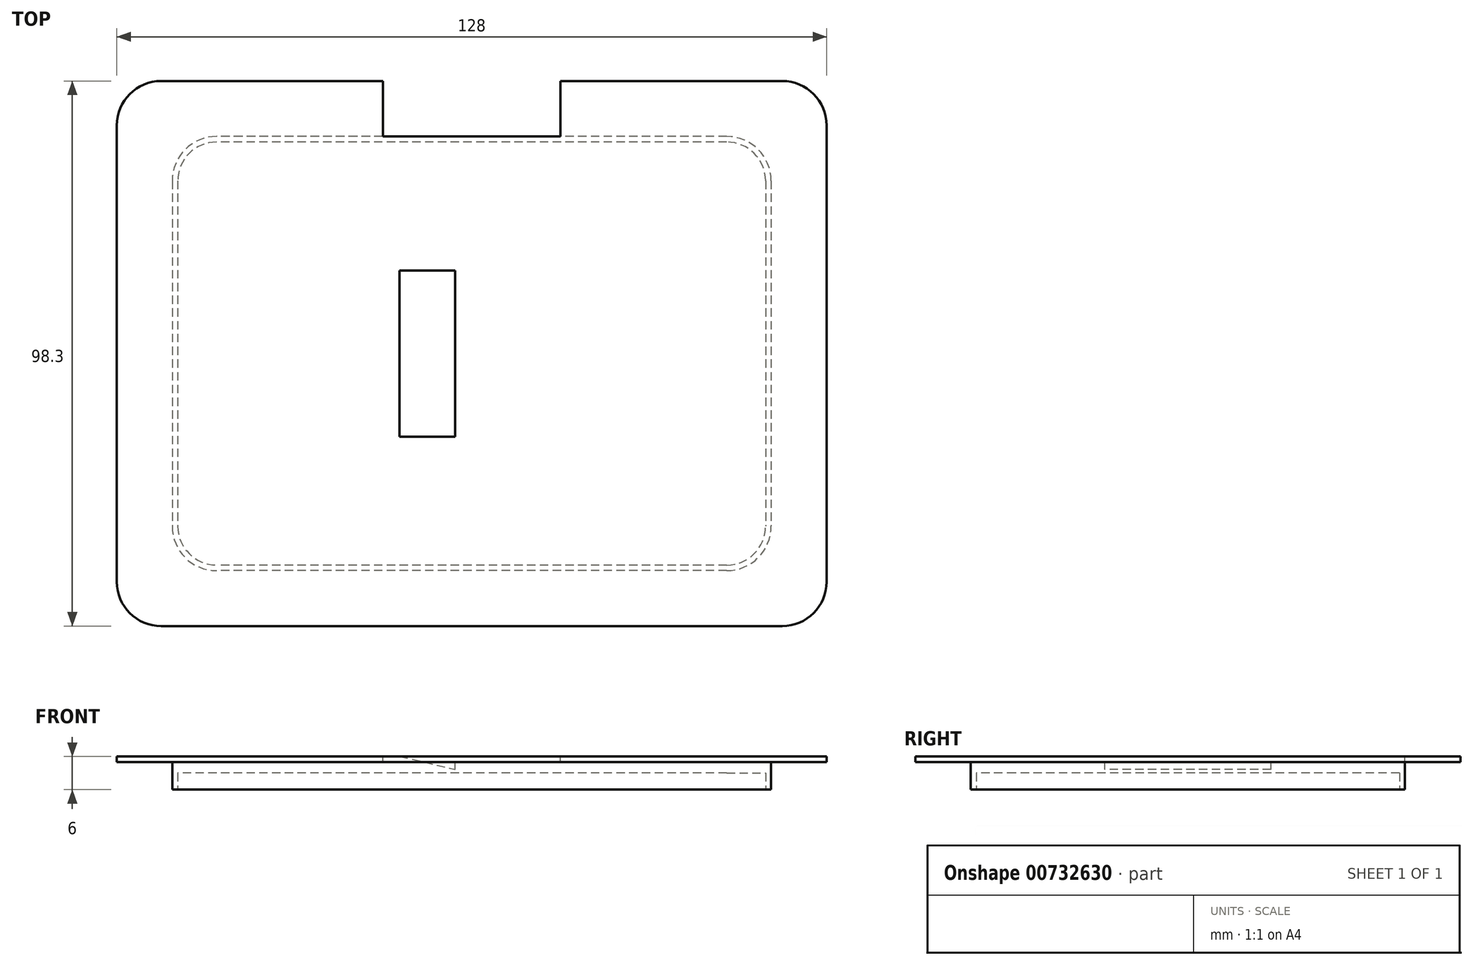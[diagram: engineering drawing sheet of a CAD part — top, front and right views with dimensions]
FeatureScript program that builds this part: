
annotation { "Feature Type Name" : "Feature", "Feature Type Description" : "" }
export const myFeature = defineFeature(function(context is Context, id is Id, definition is map)
    precondition{}
    {
        {
            var Q0;
            Q0=qCreatedBy(makeId("Top.planeOp"),FACE);
            var sketch = newSketch(context, id + "F0", { "sketchPlane" : qUnion([Q0])});
            skLineSegment(sketch, "E0.bottom", {"start": v(54, 39.15) * mm, "end": v(-54, 39.15) * mm});
            skLineSegment(sketch, "E0.top", {"start": v(54, -39.15) * mm, "end": v(-54, -39.15) * mm});
            skLineSegment(sketch, "E0.left", {"start": v(54, 39.15) * mm, "end": v(54, -39.15) * mm});
            skLineSegment(sketch, "E0.right", {"start": v(-54, 39.15) * mm, "end": v(-54, -39.15) * mm});
            skPoint(sketch, "E0.middle", {"position": v(0, 0) * mm});
            skLineSegment(sketch, "E1.0", {"start": v(64, 49.15) * mm, "end": v(-64, 49.15) * mm});
            skLineSegment(sketch, "E1.1", {"start": v(64, 49.15) * mm, "end": v(64, -49.15) * mm});
            skLineSegment(sketch, "E1.2", {"start": v(64, -49.15) * mm, "end": v(-64, -49.15) * mm});
            skLineSegment(sketch, "E1.3", {"start": v(-64, 49.15) * mm, "end": v(-64, -49.15) * mm});
            skLineSegment(sketch, "E2.bottom", {"start": v(-3, 15) * mm, "end": v(-13, 15) * mm});
            skLineSegment(sketch, "E2.top", {"start": v(-3, -15) * mm, "end": v(-13, -15) * mm});
            skLineSegment(sketch, "E2.left", {"start": v(-3, 15) * mm, "end": v(-3, -15) * mm});
            skLineSegment(sketch, "E2.right", {"start": v(-13, 15) * mm, "end": v(-13, -15) * mm});
            skPoint(sketch, "E2.middle", {"position": v(-8, 0) * mm});
            skSolve(sketch);
        }
        {
            var Q0;
            Q0=makeQuery(id+"F0.imprint","IMPRINT",FACE,{"disambiguationData":[TD([[makeQuery(id+"F0.imprint","IMPRINT",EDGE,{"derivedFrom":sQuery(id+"F0.wireOp",EDGE,"E0.bottom")}),-1.0]])]});
            var Q1;
            Q1=makeQuery(id+"F0.imprint","IMPRINT",FACE,{"disambiguationData":[TD([[makeQuery(id+"F0.imprint","IMPRINT",EDGE,{"derivedFrom":sQuery(id+"F0.wireOp",EDGE,"E0.bottom")}),1.0]])]});
            var Q2;
            Q2=makeQuery(id+"F0.imprint","IMPRINT",FACE,{"disambiguationData":[TD([[makeQuery(id+"F0.imprint","IMPRINT",EDGE,{"derivedFrom":sQuery(id+"F0.wireOp",EDGE,"E2.bottom")}),1.0]])]});
            extrude(context, id + "F1", {"entities" : qUnion([Q0, Q1, Q2]), "depth" : 1 * mm, "offsetDistance" : 25 * mm});
        }
        {
            var Q0;
            Q0=makeQuery(id+"F0.imprint","IMPRINT",FACE,{"disambiguationData":[TD([[makeQuery(id+"F0.imprint","IMPRINT",EDGE,{"derivedFrom":sQuery(id+"F0.wireOp",EDGE,"E0.bottom")}),1.0]])]});
            var Q1;
            Q1=makeQuery(id+"F0.imprint","IMPRINT",FACE,{"disambiguationData":[TD([[makeQuery(id+"F0.imprint","IMPRINT",EDGE,{"derivedFrom":sQuery(id+"F0.wireOp",EDGE,"E2.bottom")}),1.0]])]});
            extrude(context, id + "F2", {"entities" : qUnion([Q0, Q1]), "operationType" : NewBodyOperationType.ADD, "oppositeDirection" : true, "depth" : 5 * mm, "offsetDistance" : 25 * mm});
        }
        {
            var Q0;
            Q0=makeQuery(id+"F0.imprint","IMPRINT",FACE,{"disambiguationData":[TD([[makeQuery(id+"F0.imprint","IMPRINT",EDGE,{"derivedFrom":sQuery(id+"F0.wireOp",EDGE,"E2.bottom")}),1.0]])]});
            extrude(context, id + "F3", {"entities" : qUnion([Q0]), "operationType" : NewBodyOperationType.REMOVE, "endBound" : BoundingType.SYMMETRIC, "oppositeDirection" : true, "depth" : 5 * mm, "offsetDistance" : 25 * mm});
        }
        {
            var Q0;
            Q0=makeQuery(id+"F3.boolean.opBoolean","COPY",EDGE,{"derivedFrom":makeQuery(id+"F3.opExtrude","CAP_EDGE",EDGE,{"disambiguationData":[OSD([sQuery(id+"F0.wireOp",EDGE,"E2.right")])],"isStart":false})});
            chamfer(context, id + "F4", {"entities" : qUnion([Q0]), "chamferType" : ChamferType.TWO_OFFSETS, "width1" : 15 * mm, "oppositeDirection" : false, "width2" : 3.5 * mm, "tangentPropagation" : true});
        }
        {
            var Q0;
            Q0=makeQuery(id+"F2.opExtrude","CAP_FACE",FACE,{"disambiguationData":[OSD([sQuery(id+"F0.wireOp",EDGE,"E0.bottom"),sQuery(id+"F0.wireOp",EDGE,"E0.top"),sQuery(id+"F0.wireOp",EDGE,"E0.left"),sQuery(id+"F0.wireOp",EDGE,"E0.right")])],"isStart":false});
            var sketch = newSketch(context, id + "F5", { "sketchPlane" : qUnion([Q0])});
            skArc(sketch, "E3.0", {"start": v(46, -38.15) * mm, "mid": v(50.95, -36.1) * mm, "end": v(53, -31.15) * mm});
            skLineSegment(sketch, "E3.1", {"start": v(53, -31.15) * mm, "end": v(53, 31.15) * mm});
            skLineSegment(sketch, "E3.2", {"start": v(46, -38.15) * mm, "end": v(-46, -38.15) * mm});
            skArc(sketch, "E3.3", {"start": v(53, 31.15) * mm, "mid": v(50.95, 36.1) * mm, "end": v(46, 38.15) * mm});
            skArc(sketch, "E3.4", {"start": v(-53, -31.15) * mm, "mid": v(-50.95, -36.1) * mm, "end": v(-46, -38.15) * mm});
            skLineSegment(sketch, "E3.5", {"start": v(-53, -31.15) * mm, "end": v(-53, 31.15) * mm});
            skArc(sketch, "E3.6", {"start": v(-46, 38.15) * mm, "mid": v(-50.95, 36.1) * mm, "end": v(-53, 31.15) * mm});
            skLineSegment(sketch, "E3.7", {"start": v(46, 38.15) * mm, "end": v(-46, 38.15) * mm});
            skSolve(sketch);
        }
        {
            var Q0;
            Q0=makeQuery(id+"F5.imprint","IMPRINT",FACE,{"disambiguationData":[TD([[makeQuery(id+"F5.imprint","IMPRINT",EDGE,{"derivedFrom":sQuery(id+"F5.wireOp",EDGE,"E3.0")}),1.0]])]});
            extrude(context, id + "F6", {"entities" : qUnion([Q0]), "operationType" : NewBodyOperationType.REMOVE, "oppositeDirection" : true, "depth" : 3 * mm, "offsetDistance" : 25 * mm});
        }
        {
            var Q0;
            Q0=makeQuery(id+"F1.opExtrude","CAP_FACE",FACE,{"disambiguationData":[OSD([sQuery(id+"F0.wireOp",EDGE,"E1.0"),sQuery(id+"F0.wireOp",EDGE,"E1.1"),sQuery(id+"F0.wireOp",EDGE,"E1.2"),sQuery(id+"F0.wireOp",EDGE,"E1.3")])],"isStart":false});
            var sketch = newSketch(context, id + "F7", { "sketchPlane" : qUnion([Q0])});
            skPoint(sketch, "E4", {"position": v(0, 49.15) * mm});
            skLineSegment(sketch, "E5.bottom", {"start": v(-16, 49.15) * mm, "end": v(16, 49.15) * mm});
            skLineSegment(sketch, "E5.top", {"start": v(-16, 39.15) * mm, "end": v(16, 39.15) * mm});
            skLineSegment(sketch, "E5.left", {"start": v(-16, 49.15) * mm, "end": v(-16, 39.15) * mm});
            skLineSegment(sketch, "E5.right", {"start": v(16, 49.15) * mm, "end": v(16, 39.15) * mm});
            skSolve(sketch);
        }
        {
            var Q0;
            Q0=makeQuery(id+"F7.imprint","IMPRINT",FACE,{"disambiguationData":[TD([[makeQuery(id+"F7.imprint","IMPRINT",EDGE,{"derivedFrom":sQuery(id+"F7.wireOp",EDGE,"E5.bottom")}),1.0]])]});
            extrude(context, id + "F8", {"entities" : qUnion([Q0]), "operationType" : NewBodyOperationType.REMOVE, "oppositeDirection" : true, "depth" : 25 * mm, "offsetDistance" : 25 * mm});
        }
        {
            var Q0;
            Q0=makeQuery(id+"F2.opExtrude","SWEPT_EDGE",EDGE,{"disambiguationData":[OSD([sQuery(id+"F0.wireOp",EDGE,"E0.top"),sQuery(id+"F0.wireOp",EDGE,"E0.right")])]});
            var Q1;
            Q1=makeQuery(id+"F1.opExtrude","SWEPT_EDGE",EDGE,{"disambiguationData":[OSD([sQuery(id+"F0.wireOp",EDGE,"E1.2"),sQuery(id+"F0.wireOp",EDGE,"E1.3")])]});
            var Q2;
            Q2=makeQuery(id+"F1.opExtrude","SWEPT_EDGE",EDGE,{"disambiguationData":[OSD([sQuery(id+"F0.wireOp",EDGE,"E1.0"),sQuery(id+"F0.wireOp",EDGE,"E1.3")])]});
            var Q3;
            Q3=makeQuery(id+"F2.opExtrude","SWEPT_EDGE",EDGE,{"disambiguationData":[OSD([sQuery(id+"F0.wireOp",EDGE,"E0.bottom"),sQuery(id+"F0.wireOp",EDGE,"E0.right")])]});
            var Q4;
            Q4=makeQuery(id+"F1.opExtrude","SWEPT_EDGE",EDGE,{"disambiguationData":[OSD([sQuery(id+"F0.wireOp",EDGE,"E1.0"),sQuery(id+"F0.wireOp",EDGE,"E1.1")])]});
            var Q5;
            Q5=makeQuery(id+"F2.opExtrude","SWEPT_EDGE",EDGE,{"disambiguationData":[OSD([sQuery(id+"F0.wireOp",EDGE,"E0.bottom"),sQuery(id+"F0.wireOp",EDGE,"E0.left")])]});
            var Q6;
            Q6=makeQuery(id+"F2.opExtrude","SWEPT_EDGE",EDGE,{"disambiguationData":[OSD([sQuery(id+"F0.wireOp",EDGE,"E0.top"),sQuery(id+"F0.wireOp",EDGE,"E0.left")])]});
            var Q7;
            Q7=makeQuery(id+"F1.opExtrude","SWEPT_EDGE",EDGE,{"disambiguationData":[OSD([sQuery(id+"F0.wireOp",EDGE,"E1.1"),sQuery(id+"F0.wireOp",EDGE,"E1.2")])]});
            fillet(context, id + "F9", {"entities" : qUnion([Q0, Q1, Q2, Q3, Q4, Q5, Q6, Q7]), "radius" : 8 * mm, "tangentPropagation" : true, "allowEdgeOverflow" : false});
        }
    });
